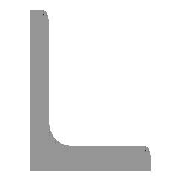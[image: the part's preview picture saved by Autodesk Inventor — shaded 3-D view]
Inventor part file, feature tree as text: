
AUTODESK INVENTOR PART (.ipt)
format: ipt  version: 2013 (Build 170138000, 138)  size: 130,048 bytes
history: native  units: mm (DEFAULTED — no unit token found)
features: other x4, plane x3, split x2, sketch x2
ambient origin geometry x8: Origin, YZ Plane, XZ Plane, XY Plane, X Axis, Y Axis, Z Axis, Center Point
bodies: Solid1 (feature_tree), Body (feature_tree)
feature tree (11):
  parser-record x1  (decoder bookkeeping rows leaked as tree rows — omitted from the tree; the rows remain in map.json)
  other  "Driven Length"
  other  "Start plane"
  other  "End plane"
  plane  "Work Plane4"
  split  "Split1"
  plane  "Work Plane5"
  split  "Split2"
  sketch  "Sketch3"  dims[d0=38.1mm]
  plane  "Work Plane3"
  sketch  "Sketch4"  dims[d1=38.1mm d2=4.7625mm d3=4.7625mm d4=1257.3mm d5=0.0mm d10=0.0mm d11=0.0mm d12=-0.0mm d13=1257.3mm d14=4.826mm d15=2.286mm d16=90.0deg d17=1257.3mm]
